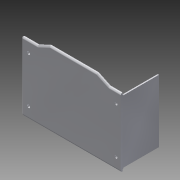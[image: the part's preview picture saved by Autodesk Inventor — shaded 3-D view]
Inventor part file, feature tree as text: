
AUTODESK INVENTOR PART (.ipt)
format: ipt  version: 2015 (Build 190159000, 159)  size: 283,136 bytes
history: native  units: in
note: dims shown in document units (in); Inventor stores cm internally (conversion verified against a paired STEP export)
features: extrude x5, reference x5, sketch x4, fillet x2, chamfer x1, other x1, projected_geometry x1
ambient origin geometry x8: Origin, YZ Plane, XZ Plane, XY Plane, X Axis, Y Axis, Z Axis, Center Point
bodies: Solid1 (feature_tree)
feature tree (19):
  extrude  "Extrusion1"  Depth=0.0591in TaperAngle=45.0deg
  chamfer  "Chamfer1"  Distance=0.3937in
  fillet  "Fillet1"  Radius=4.8709in
  fillet  "Fillet2"  Radius=1.6358in
  other  "Lip1"
  extrude  "Extrusion7"  Depth=0.0525in
  extrude  "Extrusion3"  Depth=1.5354in TaperAngle=0.0deg
  extrude  "Extrusion6"  Depth=0.3937in
  extrude  "Extrusion8"  Depth=0.3937in
  sketch  "Sketch4"  dims[d0=0.0787in d1=0.0in d4=0.0591in d5=0.0394in d6=45.0deg]
  reference  "Reference32"
  sketch  "Sketch7"  dims[d7=0.0787in]
  sketch  "Sketch8"  dims[d8=0.0394in d9=0.3937in d10=0.0in d21=4.8709in d22=1.6358in]
  projected_geometry  "Projected Loop2"
  sketch  "Sketch9"  dims[d27=0.0394in d28=0.0787in d29=0.0in d30=0.0in d31=0.0in d32=0.0in d35=0.0525in d38=1.5354in d39=0.0in d48=2.0079in d50=1.0651in d51=1.0651in d52=0.5118in d53=0.686in d54=1.0431in d55=2.8944in d56=0.5118in d57=0.0787in d58=0.5311in d59=0.0689in d60=0.1752in d61=2.6503in d62=0.0827in d63=0.0787in d64=0.1575in d65=0.0394in d66=0.0in d67=0.3937in d68=0.0in]
  reference  "Reference36"
  reference  "Reference37"
  reference  "Reference38"
  reference  "Reference39"
